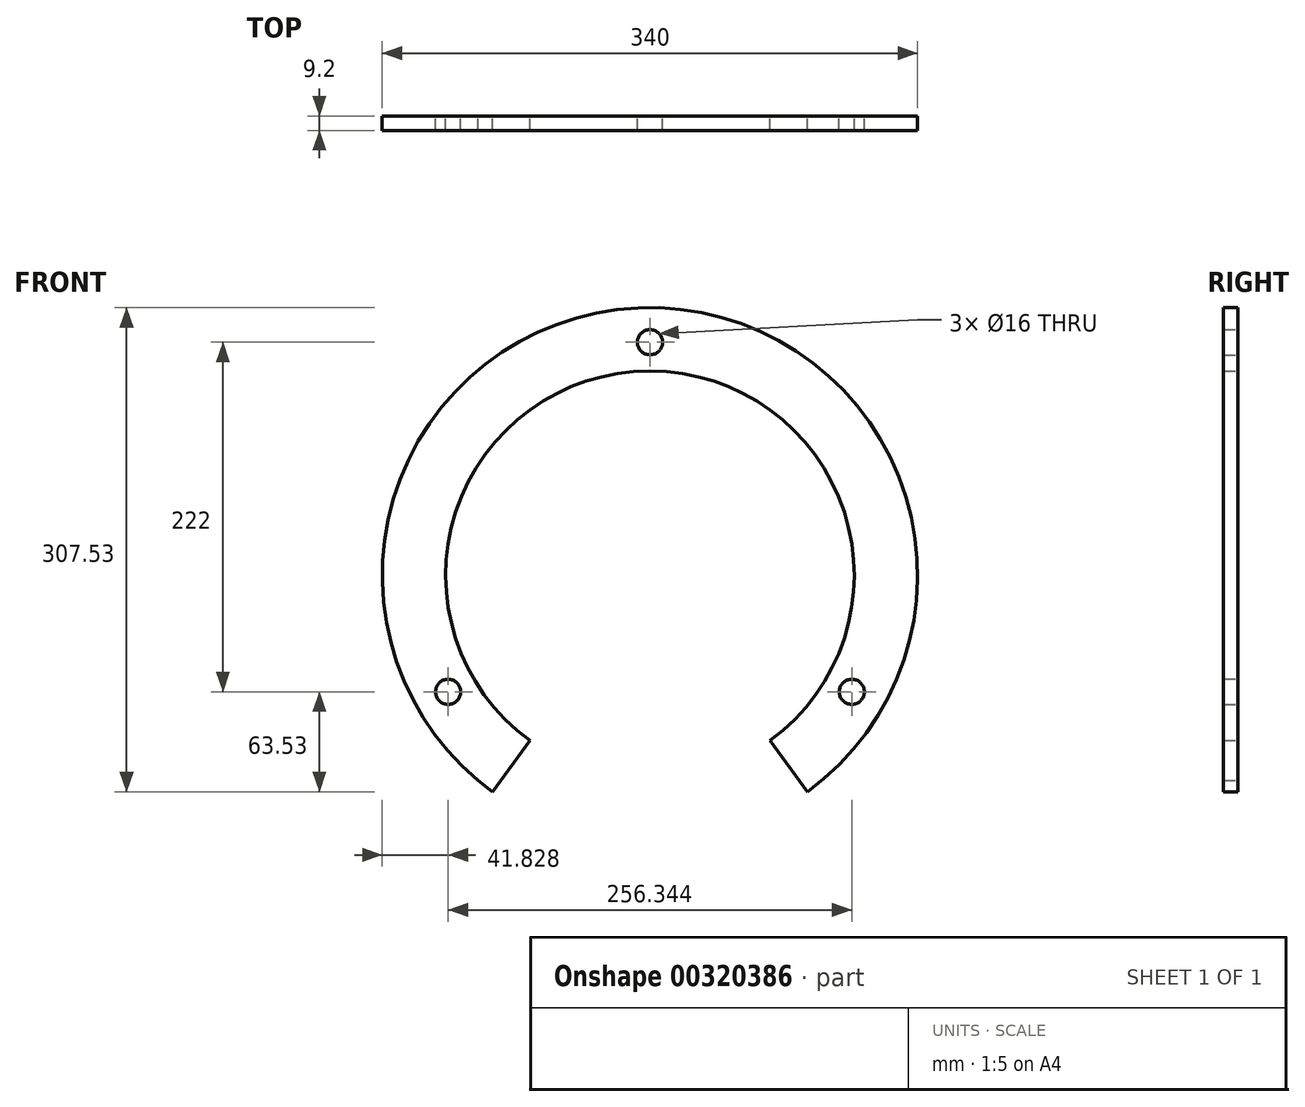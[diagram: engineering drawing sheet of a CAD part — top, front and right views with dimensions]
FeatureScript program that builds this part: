
annotation { "Feature Type Name" : "Feature", "Feature Type Description" : "" }
export const myFeature = defineFeature(function(context is Context, id is Id, definition is map)
    precondition{}
    {
        {
            var Q0;
            Q0=qCreatedBy(makeId("Front.planeOp"),FACE);
            var sketch = newSketch(context, id + "F0", { "sketchPlane" : qUnion([Q0])});
            skArc(sketch, "E0", {"start": v(99.92, -137.53) * mm, "mid": v(0, 170) * mm, "end": v(-99.92, -137.53) * mm});
            skArc(sketch, "E1", {"start": v(92.49, -91) * mm, "mid": v(-10.7, 129.3) * mm, "end": v(-76.27, -104.97) * mm});
            skLineSegment(sketch, "E2", {"start": v(0, 0) * mm, "end": v(99.92, -137.53) * mm});
            skLineSegment(sketch, "E3", {"start": v(0, 0) * mm, "end": v(-99.92, -137.53) * mm});
            skLineSegment(sketch, "E4", {"start": v(0, 0) * mm, "end": v(-109.27, -130.23) * mm, "construction": true});
            skLineSegment(sketch, "E5", {"start": v(0, 0) * mm, "end": v(109.27, -130.23) * mm, "construction": true});
            skArc(sketch, "E6", {"start": v(76.27, -104.97) * mm, "mid": v(0, 129.75) * mm, "end": v(-76.27, -104.97) * mm});
            skLineSegment(sketch, "E7", {"start": v(-109.27, -130.23) * mm, "end": v(-99.75, -137.53) * mm});
            skLineSegment(sketch, "E8", {"start": v(0, 0) * mm, "end": v(0, -129.75) * mm, "construction": true});
            skCircle(sketch, "E9", {"center": v(0, 0) * mm, "radius": 148 * mm, "construction": true});
            skLineSegment(sketch, "E10", {"start": v(0, 0) * mm, "end": v(0, 170) * mm, "construction": true});
            skLineSegment(sketch, "E11", {"start": v(0, 0) * mm, "end": v(-147.22, -85) * mm, "construction": true});
            skLineSegment(sketch, "E12", {"start": v(0, 0) * mm, "end": v(147.22, -85) * mm, "construction": true});
            skCircle(sketch, "E13", {"center": v(0, 148) * mm, "radius": 8 * mm});
            skCircle(sketch, "E14", {"center": v(-128.17, -74) * mm, "radius": 8 * mm});
            skCircle(sketch, "E15", {"center": v(128.17, -74) * mm, "radius": 8 * mm});
            skSolve(sketch);
        }
        {
            var Q0;
            {var subQ0=sQuery(id+"F0.wireOp",EDGE,"E6");var subQ3=makeQuery(id+"F0.imprint","IMPRINT",VERTEX,{"derivedFrom":subQ0});Q0=makeQuery(id+"F0.imprint","IMPRINT",FACE,{"disambiguationData":[TD([[makeQuery(id+"F0.imprint","IMPRINT",EDGE,{"disambiguationData":[TD([[subQ3,1.0]])],"derivedFrom":subQ0}),-1.0]])]});}
            extrude(context, id + "F1", {"entities" : qUnion([Q0]), "depth" : 9.2 * mm});
        }
    });
